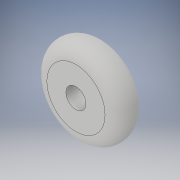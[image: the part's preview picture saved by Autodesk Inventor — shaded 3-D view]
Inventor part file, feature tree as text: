
AUTODESK INVENTOR PART (.ipt)
format: ipt  version: 2019 (Build 230136000, 136)  size: 132,608 bytes
history: native  units: in
note: dims shown in document units (in); Inventor stores cm internally (conversion verified against a paired STEP export)
features: revolve x1, sketch x1
ambient origin geometry x8: Origin, YZ Plane, XZ Plane, XY Plane, X Axis, Y Axis, Z Axis, Center Point
bodies: Solid1 (feature_tree)
feature tree (2):
  revolve  "Revolution1"  Angle=90.0deg
  sketch  "Sketch1"  dims[d0=0.8465in d3=90.0deg]
